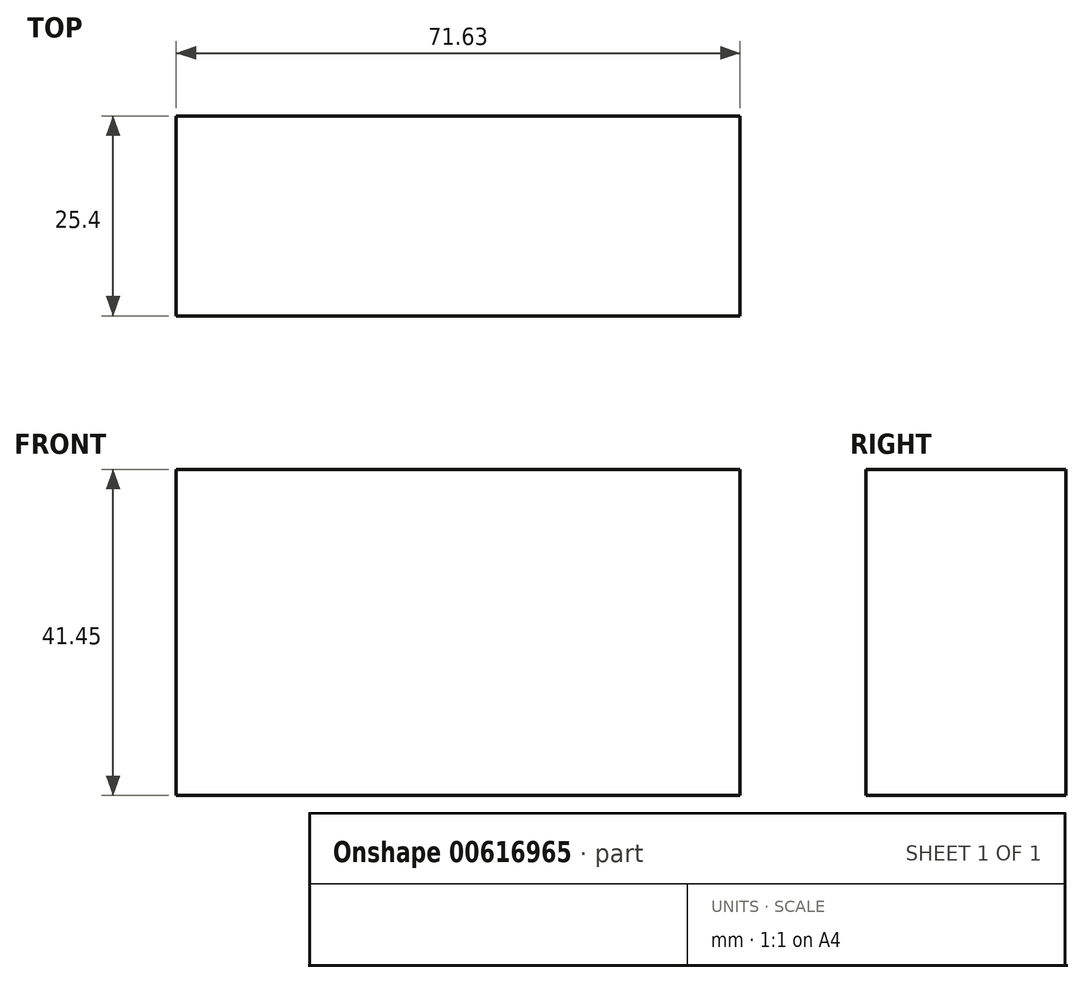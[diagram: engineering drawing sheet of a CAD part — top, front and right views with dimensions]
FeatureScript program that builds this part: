
annotation { "Feature Type Name" : "Feature", "Feature Type Description" : "" }
export const myFeature = defineFeature(function(context is Context, id is Id, definition is map)
    precondition{}
    {
        {
            var Q0;
            Q0=qCreatedBy(makeId("Front.planeOp"),FACE);
            var sketch = newSketch(context, id + "F0", { "sketchPlane" : qUnion([Q0])});
            skLineSegment(sketch, "E0", {"start": v(-34.9, -20.42) * mm, "end": v(-34.9, 21.03) * mm});
            skLineSegment(sketch, "E1", {"start": v(36.73, 21.03) * mm, "end": v(36.73, -20.42) * mm});
            skLineSegment(sketch, "E2", {"start": v(36.73, 21.03) * mm, "end": v(-34.9, 21.03) * mm});
            skLineSegment(sketch, "E3", {"start": v(-34.9, -20.42) * mm, "end": v(36.73, -20.42) * mm});
            skSolve(sketch);
        }
        {
            var Q0;
            Q0 = qSketchRegion(id + "F0", true);
            extrude(context, id + "F1", {"entities" : qUnion([Q0]), "depth" : 25.4 * mm, "offsetDistance" : 25.4 * mm});
        }
    });
